# Revit family: Accessory-Towel_Bar-KALLISTA-Vir_Stil-P80244
name_source: partatom
category: Specialty Equipment
units: mm (PartAtom-declared; Revit-internal decimal feet)

## family parameters
Cut with Voids When Loaded = No
Host = Face
OmniClass Number = 23.31.25.25
OmniClass Title = Towel Bars
Part Type = Normal
Room Calculation Point = No
Round Connector Dimension = Use Diameter
Shared = No

## types (4) — shared parameters
ADA Compliant = No
Assembly Code = C1030200
Date Modified = 10/25/2023
Default Elevation = 42"
Description = Vir Stil 24 Inch Towel Bar
Height = 2 3/16"
Length = 26 3/16"
Manufacturer = Kallista Co.
Master Format 2014 = 10 28 00
Master Format 2014 Name = Toilet, Bath, and Laundry Accessories
Material = Premium Metal Construction
Product Name = Vir Stil
URL = https://www.kallista.com
WaterSense Certified = No
Width = 3 1/8"

## per-type parameters (varying)
| type | Finish | Model | Type |
| BAF-Brushed French Gold | Kallista-Metal-BAF-Brushed_French_Gold | P80244-00-BAF | 1 |
| BN-Brushed Nickel | Kallista-Metal-BN-Brushed_Nickel | P80244-00-BN | 2 |
| CP-Chrome | Kallista-Metal-CP-Chrome | P80244-00-CP | 3 |
| SN-Polished Nickel | Kallista-Metal-SN-Polished_Nickel | P80244-00-SN | 4 |

## geometry (parser evidence)
native form markers: Sweep x6
no freeform markers — native parametric forms only
